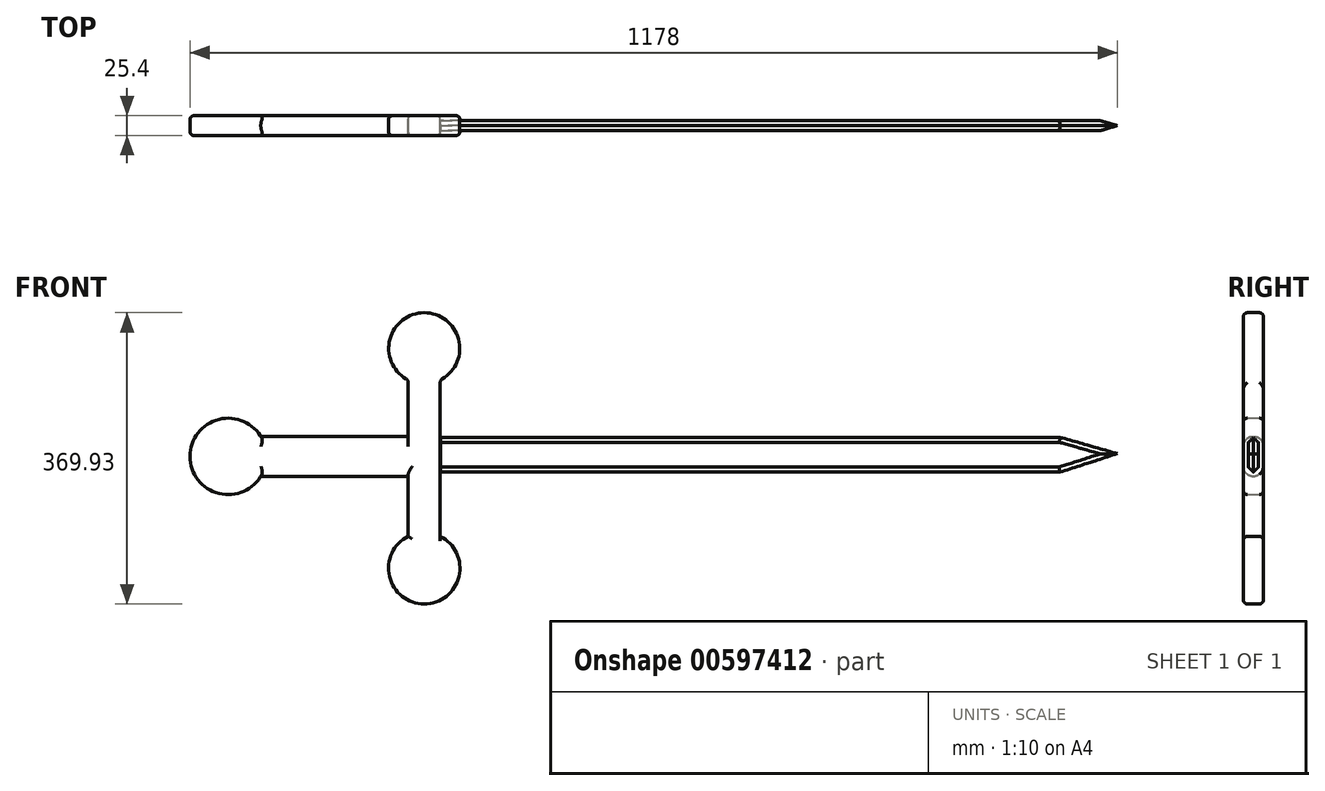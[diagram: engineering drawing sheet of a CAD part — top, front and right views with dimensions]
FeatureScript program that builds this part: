
annotation { "Feature Type Name" : "Feature", "Feature Type Description" : "" }
export const myFeature = defineFeature(function(context is Context, id is Id, definition is map)
    precondition{}
    {
        {
            var Q0;
            Q0=qCreatedBy(makeId("Front.planeOp"),FACE);
            var sketch = newSketch(context, id + "F0", { "sketchPlane" : qUnion([Q0])});
            skLineSegment(sketch, "E0.bottom", {"start": v(-643.37, 111.9) * mm, "end": v(-602.65, 111.9) * mm});
            skLineSegment(sketch, "E0.top", {"start": v(-643.37, -167.5) * mm, "end": v(-602.65, -167.5) * mm});
            skLineSegment(sketch, "E0.left", {"start": v(-643.37, 111.9) * mm, "end": v(-643.37, -167.5) * mm});
            skLineSegment(sketch, "E0.right", {"start": v(-602.65, 111.9) * mm, "end": v(-602.65, -167.5) * mm});
            skPoint(sketch, "E1", {"position": v(-623, 111.9) * mm});
            skPoint(sketch, "E2", {"position": v(-623, -167.5) * mm});
            skCircle(sketch, "E3", {"center": v(-623, -167.5) * mm, "radius": 45.36 * mm});
            skCircle(sketch, "E4", {"center": v(-623, 111.9) * mm, "radius": 45.17 * mm});
            skLineSegment(sketch, "E5.bottom", {"start": v(-643.37, 0) * mm, "end": v(-871.97, 0) * mm});
            skLineSegment(sketch, "E5.top", {"start": v(-643.37, -50.8) * mm, "end": v(-871.97, -50.8) * mm});
            skLineSegment(sketch, "E5.left", {"start": v(-643.37, 0) * mm, "end": v(-643.37, -50.8) * mm});
            skLineSegment(sketch, "E5.right", {"start": v(-871.97, 0) * mm, "end": v(-871.97, -50.8) * mm});
            skPoint(sketch, "E6", {"position": v(-871.97, -25.4) * mm});
            skCircle(sketch, "E7", {"center": v(-871.97, -25.4) * mm, "radius": 48.5 * mm});
            skSolve(sketch);
        }
        {
            var Q0;
            Q0 = qSketchRegion(id + "F0", true);
            extrude(context, id + "F1", {"entities" : qUnion([Q0]), "endBound" : BoundingType.SYMMETRIC, "depth" : 25.4 * mm, "offsetDistance" : 25.4 * mm});
        }
        {
            var Q0;
            Q0=qCreatedBy(makeId("Front.planeOp"),FACE);
            var sketch = newSketch(context, id + "F2", { "sketchPlane" : qUnion([Q0])});
            skLineSegment(sketch, "E8.bottom", {"start": v(-602.6, 0) * mm, "end": v(184.8, 0) * mm});
            skLineSegment(sketch, "E8.top", {"start": v(-602.6, -46.8) * mm, "end": v(184.8, -46.8) * mm});
            skLineSegment(sketch, "E8.left", {"start": v(-602.6, 0) * mm, "end": v(-602.6, -46.8) * mm});
            skLineSegment(sketch, "E8.right", {"start": v(184.8, 0) * mm, "end": v(184.8, -46.8) * mm});
            skFitSpline(sketch, "E9", {"points": [v(184.8, 0) * mm, v(261.9, -21.7) * mm], "startDerivative": vector(70.37, -18.72) * mm, "endDerivative": vector(70.37, -18.72) * mm});
            skFitSpline(sketch, "E10", {"points": [v(184.8, -46.8) * mm, v(261.9, -21.7) * mm], "startDerivative": vector(73.6, 25.08) * mm, "endDerivative": vector(73.6, 25.08) * mm});
            skSolve(sketch);
        }
        {
            var Q0;
            Q0 = qSketchRegion(id + "F2", true);
            extrude(context, id + "F3", {"entities" : qUnion([Q0]), "endBound" : BoundingType.SYMMETRIC, "depth" : 12.7 * mm, "offsetDistance" : 25.4 * mm});
        }
        {
            var Q0;
            Q0=makeQuery(id+"F3.opExtrude","CAP_EDGE",EDGE,{"disambiguationData":[OSD([sQuery(id+"F2.wireOp",EDGE,"E8.bottom")])],"isStart":true});
            var Q1;
            Q1=makeQuery(id+"F3.opExtrude","CAP_EDGE",EDGE,{"disambiguationData":[OSD([sQuery(id+"F2.wireOp",EDGE,"E8.top")])],"isStart":true});
            var Q2;
            Q2=makeQuery(id+"F3.opExtrude","CAP_EDGE",EDGE,{"disambiguationData":[OSD([sQuery(id+"F2.wireOp",EDGE,"E8.bottom")])],"isStart":false});
            var Q3;
            Q3=makeQuery(id+"F3.opExtrude","CAP_EDGE",EDGE,{"disambiguationData":[OSD([sQuery(id+"F2.wireOp",EDGE,"E8.top")])],"isStart":false});
            chamfer(context, id + "F4", {"entities" : qUnion([Q0, Q1, Q2, Q3]), "width" : 7.62 * mm, "tangentPropagation" : true});
        }
        {
            var Q0;
            Q0=makeQuery(id+"F3.opExtrude","CAP_EDGE",EDGE,{"disambiguationData":[OSD([sQuery(id+"F2.wireOp",EDGE,"E10")])],"isStart":true});
            var Q1;
            Q1=makeQuery(id+"F3.opExtrude","CAP_EDGE",EDGE,{"disambiguationData":[OSD([sQuery(id+"F2.wireOp",EDGE,"E10")])],"isStart":false});
            var Q2;
            Q2=makeQuery(id+"F3.opExtrude","CAP_EDGE",EDGE,{"disambiguationData":[OSD([sQuery(id+"F2.wireOp",EDGE,"E9")])],"isStart":false});
            var Q3;
            Q3=makeQuery(id+"F3.opExtrude","CAP_EDGE",EDGE,{"disambiguationData":[OSD([sQuery(id+"F2.wireOp",EDGE,"E9")])],"isStart":true});
            chamfer(context, id + "F5", {"entities" : qUnion([Q0, Q1, Q2, Q3]), "width" : 7.62 * mm, "tangentPropagation" : true});
        }
        {
            var Q0;
            Q0=makeQuery(id+"F1.opExtrude","CAP_EDGE",EDGE,{"disambiguationData":[OSD([sQuery(id+"F0.wireOp",EDGE,"E3")])],"isStart":false});
            var Q1;
            Q1=makeQuery(id+"F1.opExtrude","CAP_EDGE",EDGE,{"disambiguationData":[OSD([sQuery(id+"F0.wireOp",EDGE,"E3")])],"isStart":true});
            fillet(context, id + "F6", {"entities" : qUnion([Q0, Q1]), "radius" : 5.08 * mm, "tangentPropagation" : true, "allowEdgeOverflow" : false});
        }
        {
            var Q0;
            Q0=makeQuery(id+"F1.opExtrude","SWEPT_FACE",FACE,{"disambiguationData":[OSD([sQuery(id+"F0.wireOp",EDGE,"E4")])]});
            fillet(context, id + "F7", {"entities" : qUnion([Q0]), "radius" : 5.08 * mm, "tangentPropagation" : true, "allowEdgeOverflow" : false});
        }
        {
            var Q0;
            {var subQ0=sQuery(id+"F0.wireOp",EDGE,"E0.left");Q0=makeQuery(id+"F1.opExtrude","CAP_EDGE",EDGE,{"disambiguationData":[OSD([subQ0]),TDD([makeQuery(id+"F0.imprint","IMPRINT",EDGE,{"disambiguationData":[TD([[makeQuery(id+"F0.imprint","INTERSECT",VERTEX,{"derivedFrom":[subQ0,sQuery(id+"F0.wireOp",EDGE,"E3")]}),1.0]])],"derivedFrom":subQ0})])],"isStart":true});}
            var Q1;
            {var subQ0=sQuery(id+"F0.wireOp",EDGE,"E0.left");Q1=makeQuery(id+"F1.opExtrude","CAP_EDGE",EDGE,{"disambiguationData":[OSD([subQ0]),TDD([makeQuery(id+"F0.imprint","IMPRINT",EDGE,{"disambiguationData":[TD([[makeQuery(id+"F0.imprint","INTERSECT",VERTEX,{"derivedFrom":[subQ0,sQuery(id+"F0.wireOp",EDGE,"E3")]}),1.0]])],"derivedFrom":subQ0})])],"isStart":false});}
            fillet(context, id + "F8", {"entities" : qUnion([Q0, Q1]), "radius" : 5.08 * mm, "tangentPropagation" : true, "allowEdgeOverflow" : false});
        }
        {
            var Q0;
            Q0=makeQuery(id+"F1.opExtrude","CAP_EDGE",EDGE,{"disambiguationData":[OSD([sQuery(id+"F0.wireOp",EDGE,"E7")])],"isStart":false});
            var Q1;
            Q1=makeQuery(id+"F1.opExtrude","CAP_EDGE",EDGE,{"disambiguationData":[OSD([sQuery(id+"F0.wireOp",EDGE,"E7")])],"isStart":true});
            fillet(context, id + "F9", {"entities" : qUnion([Q0, Q1]), "radius" : 5.08 * mm, "tangentPropagation" : true, "allowEdgeOverflow" : false});
        }
        {
            var Q0;
            Q0=makeQuery(id+"F1.opExtrude","CAP_EDGE",EDGE,{"disambiguationData":[OSD([sQuery(id+"F0.wireOp",EDGE,"E5.bottom")])],"isStart":true});
            var Q1;
            Q1=makeQuery(id+"F1.opExtrude","CAP_EDGE",EDGE,{"disambiguationData":[OSD([sQuery(id+"F0.wireOp",EDGE,"E5.top")])],"isStart":true});
            var Q2;
            Q2=makeQuery(id+"F1.opExtrude","CAP_EDGE",EDGE,{"disambiguationData":[OSD([sQuery(id+"F0.wireOp",EDGE,"E5.top")])],"isStart":false});
            var Q3;
            Q3=makeQuery(id+"F1.opExtrude","CAP_EDGE",EDGE,{"disambiguationData":[OSD([sQuery(id+"F0.wireOp",EDGE,"E5.bottom")])],"isStart":false});
            fillet(context, id + "F10", {"entities" : qUnion([Q0, Q1, Q2, Q3]), "radius" : 12.7 * mm, "tangentPropagation" : true, "allowEdgeOverflow" : false});
        }
    });
